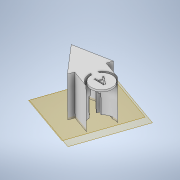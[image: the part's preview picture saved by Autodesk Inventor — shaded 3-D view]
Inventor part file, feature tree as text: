
AUTODESK INVENTOR PART (.ipt)
format: ipt  version: 2022.3 (Build 263350000, 350)  size: 235,008 bytes
history: native  units: mm
features: reference x6, sketch x5, extrude x4, plane x2, projected_geometry x2, other x2, emboss x1
ambient origin geometry x8: Origin, YZ Plane, XZ Plane, XY Plane, X Axis, Y Axis, Z Axis, Center Point
bodies: Solid1 (feature_tree)
feature tree (22):
  plane  "Work Plane1"
  extrude  "Extrusion1"  Depth=1.0mm
  plane  "Work Plane2"
  extrude  "Extrusion2"  Depth=20.0mm TaperAngle=0.0deg
  extrude  "Extrusion3"  Depth=22.0mm
  extrude  "Extrusion4"  Depth=22.0mm
  emboss  "Emboss1"
  sketch  "Sketch1"  dims[d0=42.0mm d1=0.0mm d2=1.0mm]
  reference  "Reference1"
  sketch  "Sketch2"  dims[d3=20.0mm d4=0.0mm d5=20.0mm d6=0.0mm]
  reference  "Reference2"
  sketch  "Sketch3"  dims[d7=2.0mm d8=0.0mm d9=22.0mm]
  projected_geometry  "Projected Loop1"
  reference  "Reference3"
  projected_geometry  "Projected Loop2"
  sketch  "Sketch4"  dims[d10=22.0mm d11=22.0mm]
  reference  "Reference4"
  reference  "Reference5"
  reference  "Reference6"
  sketch  "Sketch5"  dims[d12=22.0mm d13=0.0mm d14=0.0mm d15=1.0mm d16=0.0mm d23=4.0mm]
  other  "v3.0.iam"
  other  "Base:1"
